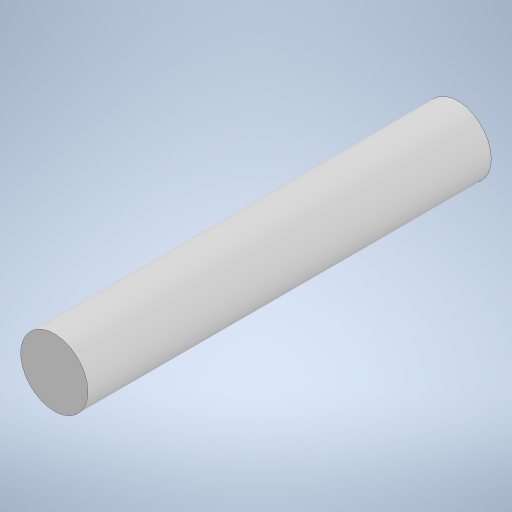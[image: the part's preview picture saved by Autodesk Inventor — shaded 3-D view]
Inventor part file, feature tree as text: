
AUTODESK INVENTOR PART (.ipt)
format: ipt  version: 2023 (Build 270158030, 158C)  size: 217,088 bytes
history: native  units: mm
features: extrude x1, sketch x1
ambient origin geometry x8: Origin, YZ Plane, XZ Plane, XY Plane, X Axis, Y Axis, Z Axis, Center Point
bodies: Solid1 (feature_tree)
feature tree (2):
  extrude  "Extrusion1"  Depth=15.0mm TaperAngle=0.0deg
  sketch  "Sketch1"  dims[d0=2.5mm d1=15.0mm d2=0.0mm]
